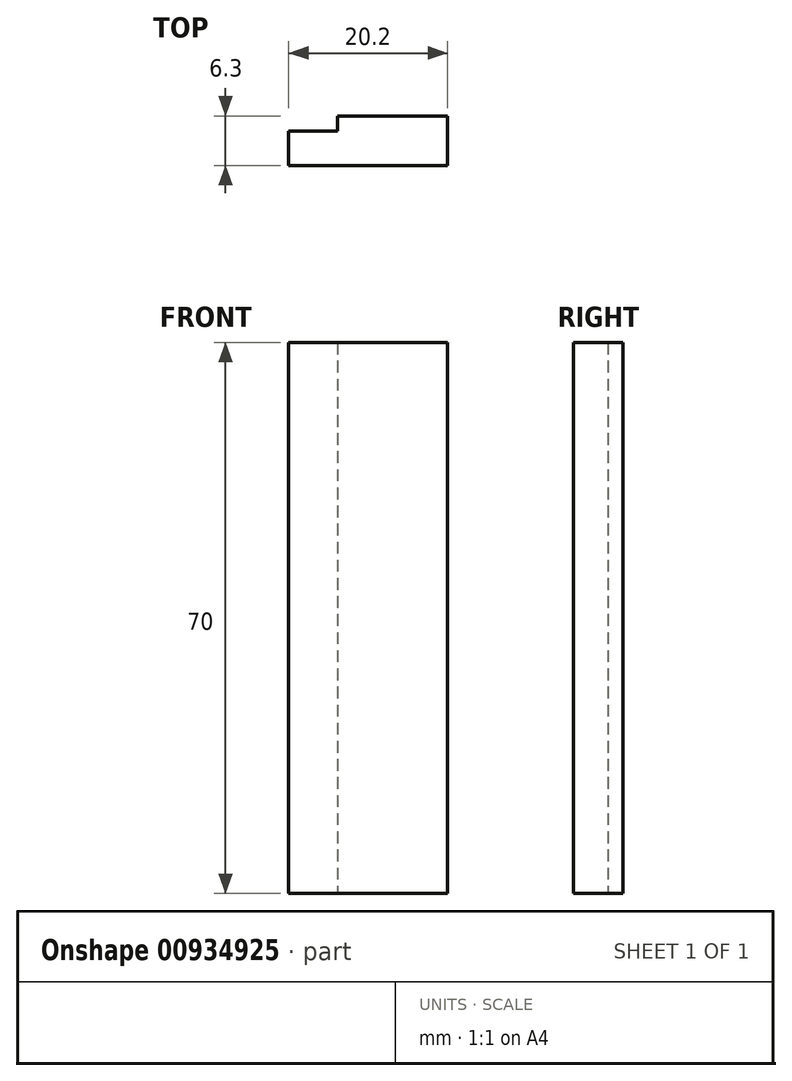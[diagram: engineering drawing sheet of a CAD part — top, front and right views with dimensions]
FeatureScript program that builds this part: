
annotation { "Feature Type Name" : "Feature", "Feature Type Description" : "" }
export const myFeature = defineFeature(function(context is Context, id is Id, definition is map)
    precondition{}
    {
        {
            var Q0;
            Q0=qCreatedBy(makeId("Top.planeOp"),FACE);
            var sketch = newSketch(context, id + "F0", { "sketchPlane" : qUnion([Q0])});
            skLineSegment(sketch, "E0", {"start": v(-10.76, 4.4) * mm, "end": v(-10.76, 0) * mm});
            skLineSegment(sketch, "E1", {"start": v(-10.76, 0) * mm, "end": v(9.44, 0) * mm});
            skLineSegment(sketch, "E2", {"start": v(9.44, 0) * mm, "end": v(9.44, 6.3) * mm});
            skLineSegment(sketch, "E3", {"start": v(9.44, 6.3) * mm, "end": v(-4.56, 6.3) * mm});
            skLineSegment(sketch, "E4", {"start": v(-4.56, 6.3) * mm, "end": v(-4.56, 4.4) * mm});
            skLineSegment(sketch, "E5", {"start": v(-4.56, 4.4) * mm, "end": v(-10.76, 4.4) * mm});
            skSolve(sketch);
        }
        {
            var Q0;
            Q0 = qSketchRegion(id + "F0", true);
            extrude(context, id + "F1", {"entities" : qUnion([Q0]), "depth" : 70 * mm, "offsetDistance" : 25 * mm});
        }
    });
